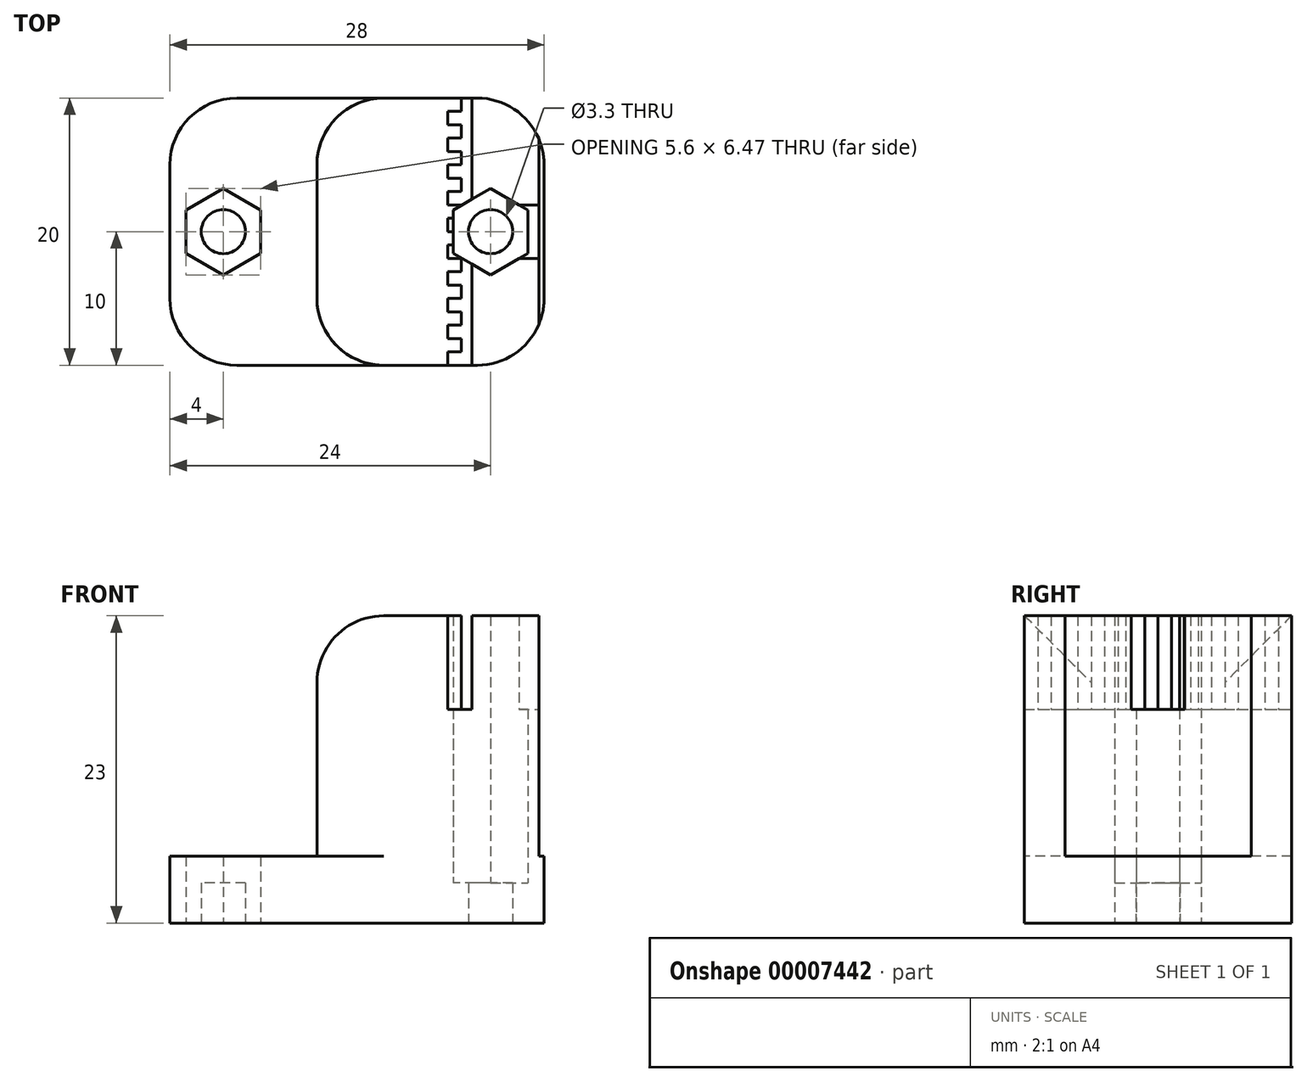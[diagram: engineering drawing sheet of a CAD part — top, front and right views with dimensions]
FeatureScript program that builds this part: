
annotation { "Feature Type Name" : "Feature", "Feature Type Description" : "" }
export const myFeature = defineFeature(function(context is Context, id is Id, definition is map)
    precondition{}
    {
        {
            var Q0;
            Q0=qCreatedBy(makeId("Top.planeOp"),FACE);
            var sketch = newSketch(context, id + "F0", { "sketchPlane" : qUnion([Q0])});
            skLineSegment(sketch, "E0", {"start": v(0, 0) * mm, "end": v(14, 0) * mm});
            skLineSegment(sketch, "E1", {"start": v(14, 0) * mm, "end": v(14, -20) * mm});
            skLineSegment(sketch, "E2", {"start": v(14, -20) * mm, "end": v(0, -20) * mm});
            skLineSegment(sketch, "E3", {"start": v(0, -20) * mm, "end": v(0, 0) * mm, "construction": true});
            skLineSegment(sketch, "E4.0.MirrorCS", {"start": v(0, 0) * mm, "end": v(-14, 0) * mm});
            skLineSegment(sketch, "E4.1.MirrorCS", {"start": v(-14, -20) * mm, "end": v(0, -20) * mm});
            skLineSegment(sketch, "E4.2.MirrorCS", {"start": v(-14, 0) * mm, "end": v(-14, -20) * mm});
            skLineSegment(sketch, "E5", {"start": v(0, -10) * mm, "end": v(10, -10) * mm, "construction": true});
            skCircle(sketch, "E6", {"center": v(10, -10) * mm, "radius": 1.65 * mm});
            skCircle(sketch, "E7.0.MirrorC", {"center": v(-10, -10) * mm, "radius": 1.65 * mm});
            skCircle(sketch, "E8.cCircle", {"center": v(10, -10) * mm, "radius": 2.8 * mm, "construction": true});
            skLineSegment(sketch, "E8.0", {"start": v(7.2, -11.62) * mm, "end": v(7.2, -8.38) * mm});
            skLineSegment(sketch, "E8.1", {"start": v(7.2, -8.38) * mm, "end": v(10, -6.77) * mm});
            skLineSegment(sketch, "E8.2", {"start": v(10, -6.77) * mm, "end": v(12.8, -8.38) * mm});
            skLineSegment(sketch, "E8.3", {"start": v(12.8, -8.38) * mm, "end": v(12.8, -11.62) * mm});
            skLineSegment(sketch, "E8.4", {"start": v(12.8, -11.62) * mm, "end": v(10, -13.23) * mm});
            skLineSegment(sketch, "E8.5", {"start": v(10, -13.23) * mm, "end": v(7.2, -11.62) * mm});
            skPoint(sketch, "E8.0.midPoint", {"position": v(7.2, -10) * mm});
            skLineSegment(sketch, "E9.0.MirrorCS", {"start": v(-10, -13.23) * mm, "end": v(-7.2, -11.62) * mm});
            skLineSegment(sketch, "E9.1.MirrorCS", {"start": v(-7.2, -11.62) * mm, "end": v(-7.2, -8.38) * mm});
            skLineSegment(sketch, "E9.2.MirrorCS", {"start": v(-7.2, -8.38) * mm, "end": v(-10, -6.77) * mm});
            skLineSegment(sketch, "E9.3.MirrorCS", {"start": v(-10, -6.77) * mm, "end": v(-12.8, -8.38) * mm});
            skLineSegment(sketch, "E9.4.MirrorCS", {"start": v(-12.8, -11.62) * mm, "end": v(-10, -13.23) * mm});
            skLineSegment(sketch, "E9.5.MirrorCS", {"start": v(-12.8, -8.38) * mm, "end": v(-12.8, -11.62) * mm});
            skSolve(sketch);
        }
        {
            var Q0;
            Q0=makeQuery(id+"F0.imprint","IMPRINT",FACE,{"disambiguationData":[TD([[makeQuery(id+"F0.imprint","IMPRINT",EDGE,{"derivedFrom":sQuery(id+"F0.wireOp",EDGE,"E0")}),-1.0]])]});
            extrude(context, id + "F1", {"entities" : qUnion([Q0]), "depth" : 5 * mm});
        }
        {
            var Q0;
            Q0=makeQuery(id+"F1.opExtrude","CAP_FACE",FACE,{"disambiguationData":[OSD([sQuery(id+"F0.wireOp",EDGE,"E0"),sQuery(id+"F0.wireOp",EDGE,"E1"),sQuery(id+"F0.wireOp",EDGE,"E2"),sQuery(id+"F0.wireOp",EDGE,"E4.0.MirrorCS"),sQuery(id+"F0.wireOp",EDGE,"E4.1.MirrorCS"),sQuery(id+"F0.wireOp",EDGE,"E4.2.MirrorCS"),sQuery(id+"F0.wireOp",EDGE,"E8.0"),sQuery(id+"F0.wireOp",EDGE,"E8.1"),sQuery(id+"F0.wireOp",EDGE,"E8.2"),sQuery(id+"F0.wireOp",EDGE,"E8.3"),sQuery(id+"F0.wireOp",EDGE,"E8.4"),sQuery(id+"F0.wireOp",EDGE,"E8.5"),sQuery(id+"F0.wireOp",EDGE,"E9.0.MirrorCS"),sQuery(id+"F0.wireOp",EDGE,"E9.1.MirrorCS"),sQuery(id+"F0.wireOp",EDGE,"E9.2.MirrorCS"),sQuery(id+"F0.wireOp",EDGE,"E9.3.MirrorCS"),sQuery(id+"F0.wireOp",EDGE,"E9.4.MirrorCS"),sQuery(id+"F0.wireOp",EDGE,"E9.5.MirrorCS")])],"isStart":false});
            var sketch = newSketch(context, id + "F2", { "sketchPlane" : qUnion([Q0])});
            skLineSegment(sketch, "E10", {"start": v(0, 0) * mm, "end": v(-3, 0) * mm});
            skLineSegment(sketch, "E11", {"start": v(-3, 0) * mm, "end": v(-3, -20) * mm});
            skLineSegment(sketch, "E12", {"start": v(6.8, 0) * mm, "end": v(0, 0) * mm});
            skLineSegment(sketch, "E13", {"start": v(6.8, 0) * mm, "end": v(8.6, 0) * mm});
            skLineSegment(sketch, "E14", {"start": v(8.6, 0) * mm, "end": v(8.6, -8) * mm});
            skLineSegment(sketch, "E15", {"start": v(8.6, -8) * mm, "end": v(8.6, -12) * mm, "construction": true});
            skLineSegment(sketch, "E16", {"start": v(8.6, -12) * mm, "end": v(8.6, -20) * mm});
            skLineSegment(sketch, "E17", {"start": v(8.6, -20) * mm, "end": v(13.6, -20) * mm});
            skLineSegment(sketch, "E18", {"start": v(13.6, -20) * mm, "end": v(13.6, -12) * mm});
            skLineSegment(sketch, "E19", {"start": v(13.6, -12) * mm, "end": v(8.6, -12) * mm});
            skLineSegment(sketch, "E20", {"start": v(8.6, -8) * mm, "end": v(13.6, -8) * mm});
            skLineSegment(sketch, "E21", {"start": v(13.6, -8) * mm, "end": v(13.6, 0) * mm});
            skLineSegment(sketch, "E22", {"start": v(13.6, 0) * mm, "end": v(8.6, 0) * mm});
            skLineSegment(sketch, "E23", {"start": v(13.6, -8) * mm, "end": v(13.6, -12) * mm});
            skLineSegment(sketch, "E24", {"start": v(6.8, 0) * mm, "end": v(7.8, 0) * mm});
            skLineSegment(sketch, "E25", {"start": v(7.8, 0) * mm, "end": v(7.8, -1) * mm});
            skLineSegment(sketch, "E26", {"start": v(7.8, -1) * mm, "end": v(6.8, -1) * mm});
            skLineSegment(sketch, "E27", {"start": v(6.8, -1) * mm, "end": v(6.8, -2) * mm});
            skLineSegment(sketch, "E28", {"start": v(6.8, -1) * mm, "end": v(6.8, 0) * mm, "construction": true});
            skLineSegment(sketch, "E29.1.0.0", {"start": v(6.8, -3) * mm, "end": v(6.8, -4) * mm});
            skLineSegment(sketch, "E29.1.0.1", {"start": v(7.8, -3) * mm, "end": v(6.8, -3) * mm});
            skLineSegment(sketch, "E29.1.0.2", {"start": v(7.8, -2) * mm, "end": v(7.8, -3) * mm});
            skLineSegment(sketch, "E29.1.0.3", {"start": v(6.8, -2) * mm, "end": v(7.8, -2) * mm});
            skLineSegment(sketch, "E29.2.0.0", {"start": v(6.8, -5) * mm, "end": v(6.8, -6) * mm});
            skLineSegment(sketch, "E29.2.0.1", {"start": v(7.8, -5) * mm, "end": v(6.8, -5) * mm});
            skLineSegment(sketch, "E29.2.0.2", {"start": v(7.8, -4) * mm, "end": v(7.8, -5) * mm});
            skLineSegment(sketch, "E29.2.0.3", {"start": v(6.8, -4) * mm, "end": v(7.8, -4) * mm});
            skLineSegment(sketch, "E29.3.0.0", {"start": v(6.8, -7) * mm, "end": v(6.8, -8) * mm});
            skLineSegment(sketch, "E29.3.0.1", {"start": v(7.8, -7) * mm, "end": v(6.8, -7) * mm});
            skLineSegment(sketch, "E29.3.0.2", {"start": v(7.8, -6) * mm, "end": v(7.8, -7) * mm});
            skLineSegment(sketch, "E29.3.0.3", {"start": v(6.8, -6) * mm, "end": v(7.8, -6) * mm});
            skLineSegment(sketch, "E29.4.0.0", {"start": v(6.8, -9) * mm, "end": v(6.8, -10) * mm});
            skLineSegment(sketch, "E29.4.0.1", {"start": v(7.8, -9) * mm, "end": v(6.8, -9) * mm});
            skLineSegment(sketch, "E29.4.0.2", {"start": v(7.8, -8) * mm, "end": v(7.8, -9) * mm});
            skLineSegment(sketch, "E29.4.0.3", {"start": v(6.8, -8) * mm, "end": v(7.8, -8) * mm});
            skLineSegment(sketch, "E29.5.0.0", {"start": v(6.8, -11) * mm, "end": v(6.8, -12) * mm});
            skLineSegment(sketch, "E29.5.0.1", {"start": v(7.8, -11) * mm, "end": v(6.8, -11) * mm});
            skLineSegment(sketch, "E29.5.0.2", {"start": v(7.8, -10) * mm, "end": v(7.8, -11) * mm});
            skLineSegment(sketch, "E29.5.0.3", {"start": v(6.8, -10) * mm, "end": v(7.8, -10) * mm});
            skLineSegment(sketch, "E29.6.0.0", {"start": v(6.8, -13) * mm, "end": v(6.8, -14) * mm});
            skLineSegment(sketch, "E29.6.0.1", {"start": v(7.8, -13) * mm, "end": v(6.8, -13) * mm});
            skLineSegment(sketch, "E29.6.0.2", {"start": v(7.8, -12) * mm, "end": v(7.8, -13) * mm});
            skLineSegment(sketch, "E29.6.0.3", {"start": v(6.8, -12) * mm, "end": v(7.8, -12) * mm});
            skLineSegment(sketch, "E29.7.0.0", {"start": v(6.8, -15) * mm, "end": v(6.8, -16) * mm});
            skLineSegment(sketch, "E29.7.0.1", {"start": v(7.8, -15) * mm, "end": v(6.8, -15) * mm});
            skLineSegment(sketch, "E29.7.0.2", {"start": v(7.8, -14) * mm, "end": v(7.8, -15) * mm});
            skLineSegment(sketch, "E29.7.0.3", {"start": v(6.8, -14) * mm, "end": v(7.8, -14) * mm});
            skLineSegment(sketch, "E29.8.0.0", {"start": v(6.8, -17) * mm, "end": v(6.8, -18) * mm});
            skLineSegment(sketch, "E29.8.0.1", {"start": v(7.8, -17) * mm, "end": v(6.8, -17) * mm});
            skLineSegment(sketch, "E29.8.0.2", {"start": v(7.8, -16) * mm, "end": v(7.8, -17) * mm});
            skLineSegment(sketch, "E29.8.0.3", {"start": v(6.8, -16) * mm, "end": v(7.8, -16) * mm});
            skLineSegment(sketch, "E29.9.0.0", {"start": v(6.8, -19) * mm, "end": v(6.8, -20) * mm});
            skLineSegment(sketch, "E29.9.0.1", {"start": v(7.8, -19) * mm, "end": v(6.8, -19) * mm});
            skLineSegment(sketch, "E29.9.0.2", {"start": v(7.8, -18) * mm, "end": v(7.8, -19) * mm});
            skLineSegment(sketch, "E29.9.0.3", {"start": v(6.8, -18) * mm, "end": v(7.8, -18) * mm});
            skLineSegment(sketch, "E29.direction1", {"start": v(6.8, -2) * mm, "end": v(6.8, -4) * mm, "construction": true});
            skLineSegment(sketch, "E30", {"start": v(6.8, -20) * mm, "end": v(-3, -20) * mm});
            skLineSegment(sketch, "E31", {"start": v(8.6, -20) * mm, "end": v(6.8, -20) * mm});
            skSolve(sketch);
        }
        {
            var Q0;
            {var subQ6=sQuery(id+"F2.wireOp",EDGE,"E25");Q0=makeQuery(id+"F2.imprint","IMPRINT",FACE,{"disambiguationData":[TD([[makeQuery(id+"F2.imprint","IMPRINT",EDGE,{"derivedFrom":subQ6}),1.0]])]});}
            var Q1;
            {var subQ8=sQuery(id+"F2.wireOp",EDGE,"E21");Q1=makeQuery(id+"F2.imprint","IMPRINT",FACE,{"disambiguationData":[TD([[makeQuery(id+"F2.imprint","IMPRINT",EDGE,{"derivedFrom":subQ8}),1.0]])]});}
            var Q2;
            {var subQ8=sQuery(id+"F2.wireOp",EDGE,"E29.5.0.0");Q2=makeQuery(id+"F2.imprint","IMPRINT",FACE,{"disambiguationData":[TD([[makeQuery(id+"F2.imprint","IMPRINT",EDGE,{"derivedFrom":subQ8}),1.0]])]});}
            var Q3;
            Q3=makeQuery(id+"F2.imprint","IMPRINT",FACE,{"disambiguationData":[TD([[makeQuery(id+"F2.imprint","IMPRINT",EDGE,{"derivedFrom":sQuery(id+"F2.wireOp",EDGE,"E10")}),-1.0]])]});
            var Q4;
            {var subQ8=sQuery(id+"F2.wireOp",EDGE,"E17");Q4=makeQuery(id+"F2.imprint","IMPRINT",FACE,{"disambiguationData":[TD([[makeQuery(id+"F2.imprint","IMPRINT",EDGE,{"derivedFrom":subQ8}),1.0]])]});}
            var Q5;
            {var subQ7=sQuery(id+"F2.wireOp",EDGE,"E23");Q5=makeQuery(id+"F2.imprint","IMPRINT",FACE,{"disambiguationData":[TD([[makeQuery(id+"F2.imprint","IMPRINT",EDGE,{"derivedFrom":subQ7}),-1.0]])]});}
            var Q6;
            {var subQ5=sQuery(id+"F2.wireOp",EDGE,"E29.4.0.0");Q6=makeQuery(id+"F2.imprint","IMPRINT",FACE,{"disambiguationData":[TD([[makeQuery(id+"F2.imprint","IMPRINT",EDGE,{"derivedFrom":subQ5}),1.0]])]});}
            extrude(context, id + "F3", {"entities" : qUnion([Q0, Q1, Q2, Q3, Q4, Q5, Q6]), "operationType" : NewBodyOperationType.ADD, "depth" : (16 - 5) * mm});
        }
        {
            var Q0;
            Q0=makeQuery(id+"F2.imprint","IMPRINT",FACE,{"disambiguationData":[TD([[makeQuery(id+"F2.imprint","IMPRINT",EDGE,{"derivedFrom":sQuery(id+"F2.wireOp",EDGE,"E10")}),-1.0]])]});
            var Q1;
            {var subQ8=sQuery(id+"F2.wireOp",EDGE,"E21");Q1=makeQuery(id+"F2.imprint","IMPRINT",FACE,{"disambiguationData":[TD([[makeQuery(id+"F2.imprint","IMPRINT",EDGE,{"derivedFrom":subQ8}),1.0]])]});}
            var Q2;
            {var subQ8=sQuery(id+"F2.wireOp",EDGE,"E17");Q2=makeQuery(id+"F2.imprint","IMPRINT",FACE,{"disambiguationData":[TD([[makeQuery(id+"F2.imprint","IMPRINT",EDGE,{"derivedFrom":subQ8}),1.0]])]});}
            extrude(context, id + "F4", {"entities" : qUnion([Q0, Q1, Q2]), "operationType" : NewBodyOperationType.ADD, "depth" : (16 - 5 + 7) * mm});
        }
        {
            var Q0;
            Q0=makeQuery(id+"F0.imprint","IMPRINT",FACE,{"disambiguationData":[TD([[makeQuery(id+"F0.imprint","IMPRINT",EDGE,{"derivedFrom":sQuery(id+"F0.wireOp",EDGE,"E7.0.MirrorC")}),1.0]])]});
            var Q1;
            Q1=makeQuery(id+"F0.imprint","IMPRINT",FACE,{"disambiguationData":[TD([[makeQuery(id+"F0.imprint","IMPRINT",EDGE,{"derivedFrom":sQuery(id+"F0.wireOp",EDGE,"E6")}),-1.0]])]});
            extrude(context, id + "F5", {"entities" : qUnion([Q0, Q1]), "operationType" : NewBodyOperationType.REMOVE, "endBound" : BoundingType.THROUGH_ALL, "depth" : 12 * mm});
        }
        {
            var Q0;
            Q0=makeQuery(id+"F0.imprint","IMPRINT",FACE,{"disambiguationData":[TD([[makeQuery(id+"F0.imprint","IMPRINT",EDGE,{"derivedFrom":sQuery(id+"F0.wireOp",EDGE,"E7.0.MirrorC")}),1.0]])]});
            var Q1;
            Q1=makeQuery(id+"F0.imprint","IMPRINT",FACE,{"disambiguationData":[TD([[makeQuery(id+"F0.imprint","IMPRINT",EDGE,{"derivedFrom":sQuery(id+"F0.wireOp",EDGE,"E6")}),-1.0]])]});
            extrude(context, id + "F6", {"entities" : qUnion([Q0, Q1]), "operationType" : NewBodyOperationType.ADD, "depth" : 3 * mm});
        }
        {
            var Q0;
            Q0=makeQuery(id+"F1.opExtrude","SWEPT_EDGE",EDGE,{"disambiguationData":[OSD([sQuery(id+"F0.wireOp",EDGE,"E4.1.MirrorCS"),sQuery(id+"F0.wireOp",EDGE,"E4.2.MirrorCS")])]});
            var Q1;
            Q1=makeQuery(id+"F1.opExtrude","SWEPT_EDGE",EDGE,{"disambiguationData":[OSD([sQuery(id+"F0.wireOp",EDGE,"E1"),sQuery(id+"F0.wireOp",EDGE,"E2")])]});
            var Q2;
            Q2=makeQuery(id+"F1.opExtrude","SWEPT_EDGE",EDGE,{"disambiguationData":[OSD([sQuery(id+"F0.wireOp",EDGE,"E0"),sQuery(id+"F0.wireOp",EDGE,"E1")])]});
            var Q3;
            Q3=makeQuery(id+"F1.opExtrude","SWEPT_EDGE",EDGE,{"disambiguationData":[OSD([sQuery(id+"F0.wireOp",EDGE,"E4.0.MirrorCS"),sQuery(id+"F0.wireOp",EDGE,"E4.2.MirrorCS")])]});
            var Q4;
            Q4=makeQuery(id+"F3.opExtrude","SWEPT_EDGE",EDGE,{"disambiguationData":[OSD([sQuery(id+"F0.wireOp",EDGE,"E0"),sQuery(id+"F0.wireOp",EDGE,"E4.0.MirrorCS"),sQuery(id+"F2.wireOp",EDGE,"E10"),sQuery(id+"F2.wireOp",EDGE,"E11")])]});
            var Q5;
            Q5=makeQuery(id+"F3.opExtrude","SWEPT_EDGE",EDGE,{"disambiguationData":[OSD([sQuery(id+"F0.wireOp",EDGE,"E2"),sQuery(id+"F0.wireOp",EDGE,"E4.1.MirrorCS"),sQuery(id+"F2.wireOp",EDGE,"E11"),sQuery(id+"F2.wireOp",EDGE,"E30")])]});
            var Q6;
            Q6=makeQuery(id+"F3.opExtrude","CAP_EDGE",EDGE,{"disambiguationData":[OSD([sQuery(id+"F2.wireOp",EDGE,"E11")])],"isStart":false});
            var Q7;
            Q7=makeQuery(id+"F3.opExtrude","CAP_EDGE",EDGE,{"disambiguationData":[OSD([sQuery(id+"F2.wireOp",EDGE,"E11")])],"isStart":true});
            var Q8;
            Q8=makeQuery(id+"F4.opExtrude","CAP_EDGE",EDGE,{"disambiguationData":[OSD([sQuery(id+"F2.wireOp",EDGE,"E11")])],"isStart":false});
            fillet(context, id + "F7", {"entities" : qUnion([Q0, Q1, Q2, Q3, Q4, Q5, Q6, Q7, Q8]), "radius" : 5 * mm, "tangentPropagation" : true, "allowEdgeOverflow" : false});
        }
    });
